# Revit family: E_Cable Tray Support_MEPcontent_OBO Bettermann_US5 FT
name_source: partatom
category: Cable Tray Fittings
revit_build: Autodesk Revit MEP 2015 (Build: 20140606_1530(x64)
units: mm (PartAtom-declared; Revit-internal decimal feet)

## types (11) — shared parameters
Article Description = U support with welded head plate.
Depth = 75 mm
Description = U support with welded head plate.
EMCS Version = 2.0
ETIM Article Class = EC000082
Family Version = 10.14
Gray = Color RGB 189-187-185
IFCExportAs = IfcCableCarrierFittingType
IFCExportType = NOTDEFINED
MEPcontent Class = CABLE_TRAY_SUPPORT
Manufacturer = OBO BETTERMANN
Manufacturer URL = http://catalog4.obo-bettermann.com
Product Line = OBO BETTERMANN CableTrays
Revit Version = 2015
URL = www.stabiplan.com
Width 1 = 50 mm  [stored 0.164042 ft]

## per-type parameters (varying)
| type | GTIN | Height 1 | Manufacturer Art. No. |
| US 5 K 20 FT | 4012196536771 | 200 mm  [stored 0.656168 ft] | 6341527 |
| US 5 K 30 FT | 4012196536719 | 300 mm | 6341535 |
| US 5 K 40 FT | 4012196536658 | 400 mm  [stored 1.31234 ft] | 6341543 |
| US 5 K 50 FT | 4012196536597 | 500 mm  [stored 1.64042 ft] | 6341551 |
| US 5 K 60 FT | 4012196536535 | 600 mm | 6341578 |
| US 5 K 70 FT | 4012196536474 | 700 mm  [stored 2.29659 ft] | 6341586 |
| US 5 K 80 FT | 4012196536412 | 800 mm  [stored 2.62467 ft] | 6341594 |
| US 5 K 90 FT | 4012196536351 | 900 mm  [stored 2.95276 ft] | 6341608 |
| US 5 K 100 FT | 4012196536290 | 1000 mm  [stored 3.28084 ft] | 6341616 |
| US 5 K 110 FT | 4012196536238 | 1100 mm | 6341624 |
| US 5 K 120 FT | 4012196536177 | 1200 mm | 6341632 |

note: column(s) folded — value = type name in every type: Article Type, Model

note: [stored X ft] marks values corroborated as IEEE doubles in the binary element streams (Revit-internal decimal feet)

## geometry (parser evidence)
native form markers: Blend x4, Sweep x3
no freeform markers — native parametric forms only
